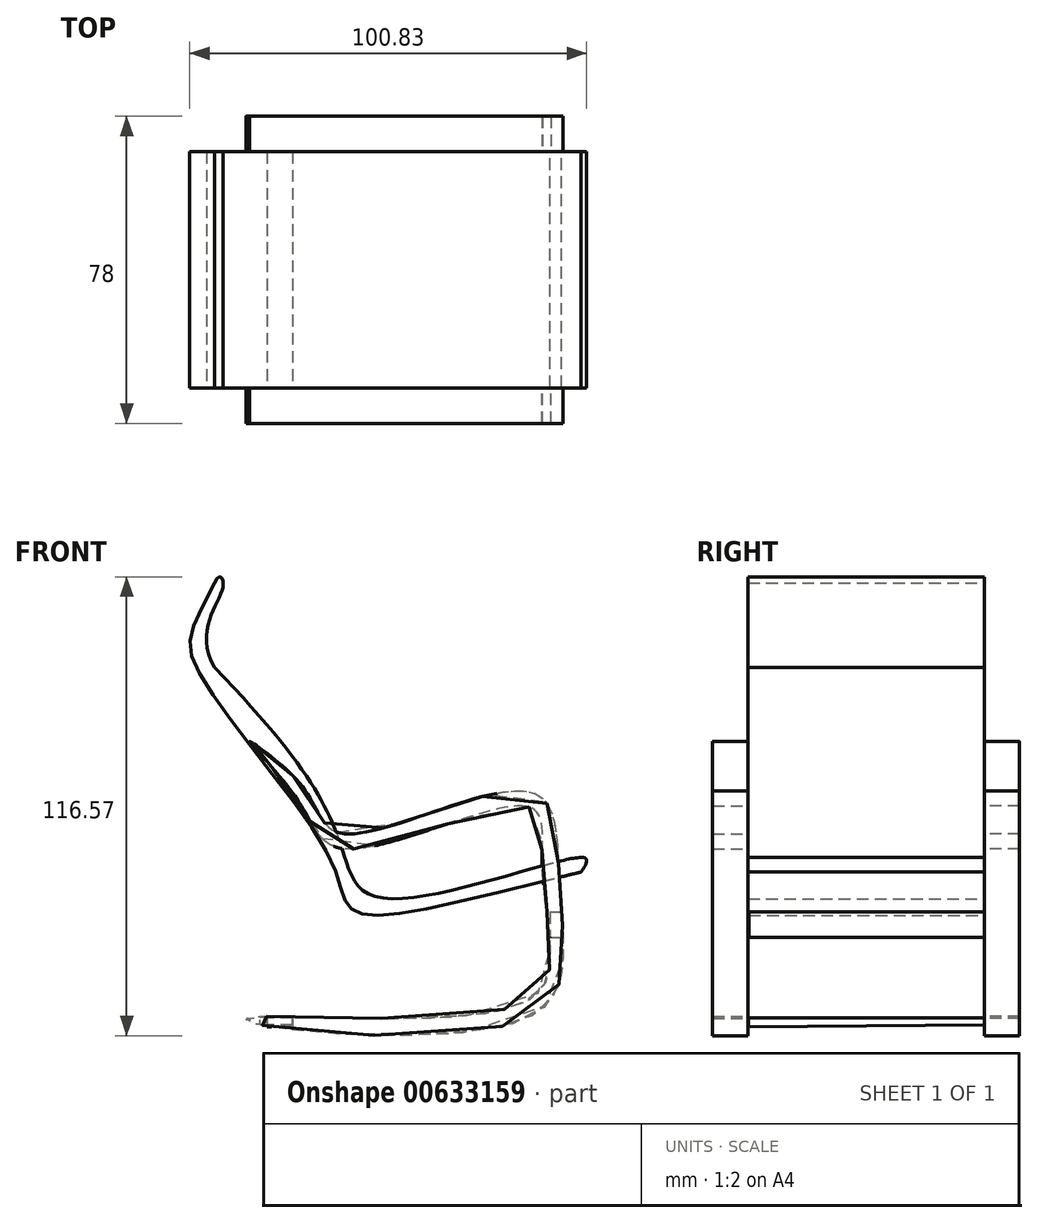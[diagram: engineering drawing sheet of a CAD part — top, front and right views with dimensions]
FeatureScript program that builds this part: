
annotation { "Feature Type Name" : "Feature", "Feature Type Description" : "" }
export const myFeature = defineFeature(function(context is Context, id is Id, definition is map)
    precondition{}
    {
        {
            var Q0;
            Q0=qCreatedBy(makeId("Front.planeOp"),FACE);
            var sketch = newSketch(context, id + "F0", { "sketchPlane" : qUnion([Q0])});
            skFitSpline(sketch, "E0", {"points": [v(-48.16, 69.9) * mm, v(-52.8, 48.36) * mm, v(-18.93, 0) * mm, v(-13.2, -13.17) * mm, v(44.92, -3.6) * mm], "startDerivative": vector(-88.69, -172.63) * mm, "endDerivative": vector(318.04, 76.89) * mm});
            skFitSpline(sketch, "E1", {"points": [v(-48.16, 69.9) * mm, v(-45.98, 69.9) * mm, v(-48.16, 48.36) * mm], "startDerivative": vector(13.48, 31.3) * mm, "endDerivative": vector(23, -40.33) * mm});
            skFitSpline(sketch, "E2", {"points": [v(-48.16, 48.36) * mm, v(-15.83, 2.51) * mm, v(-6.51, -10.03) * mm, v(43.68, 0) * mm, v(44.92, -3.6) * mm], "startDerivative": vector(188.22, -194.77) * mm, "endDerivative": vector(-82.48, -113.88) * mm});
            skSolve(sketch);
        }
        {
            var Q0;
            Q0=makeQuery(id+"F0.imprint","IMPRINT",FACE,{"disambiguationData":[TD([[makeQuery(id+"F0.imprint","IMPRINT",EDGE,{"derivedFrom":sQuery(id+"F0.wireOp",EDGE,"E0")}),1.0]])]});
            var Q1;
            Q1=sQuery(id+"F0.wireOp",EDGE,"E0");
            var Q2;
            Q2=sQuery(id+"F0.wireOp",EDGE,"E1");
            var Q3;
            Q3=sQuery(id+"F0.wireOp",EDGE,"E2");
            extrude(context, id + "F1", {"entities" : qUnion([Q0]), "surfaceEntities" : qUnion([Q1, Q2, Q3]), "depth" : 60 * mm, "offsetDistance" : 25 * mm});
        }
        {
            var Q0;
            Q0=qCreatedBy(makeId("Front.planeOp"),FACE);
            cPlane(context, id + "F2", {"entities" : qUnion([Q0]), "cplaneType" : CPlaneType.OFFSET, "offset" : 60 * mm, "width" : 150 * mm, "height" : 150 * mm});
        }
        {
            var Q0;
            Q0=qCreatedBy(id+"F2.planeOp",FACE);
            var sketch = newSketch(context, id + "F3", { "sketchPlane" : qUnion([Q0])});
            skFitSpline(sketch, "E3", {"points": [v(-38.56, 29.18) * mm, v(-25, 16.98) * mm, v(-15.26, 6.1) * mm, v(31.96, 16.75) * mm, v(39.1, 0) * mm, v(40.37, -22.89) * mm, v(30.08, -41.23) * mm, v(-39.86, -41.46) * mm, v(-39.86, -40.72) * mm, v(28.4, -37.68) * mm, v(37.18, -22.47) * mm, v(35.02, 0) * mm, v(31.8, 12.9) * mm, v(-14.68, 2.26) * mm, v(-27.1, 14.72) * mm, v(-39.28, 29.5) * mm, v(-38.56, 29.18) * mm]});
            skSolve(sketch);
        }
        {
            var Q0;
            Q0 = qSketchRegion(id + "F3", true);
            extrude(context, id + "F4", {"entities" : qUnion([Q0]), "operationType" : NewBodyOperationType.ADD, "depth" : 9 * mm, "offsetDistance" : 25 * mm});
        }
        {
            var Q0;
            Q0=qCreatedBy(makeId("Front.planeOp"),FACE);
            cPlane(context, id + "F5", {"entities" : qUnion([Q0]), "cplaneType" : CPlaneType.OFFSET, "offset" : 30 * mm, "width" : 150 * mm, "height" : 150 * mm});
        }
        {
            var Q0;
            Q0=makeQuery(id+"F1.opExtrude","SWEPT_BODY",BODY,{"disambiguationData":[OSD([sQuery(id+"F0.wireOp",EDGE,"E0"),sQuery(id+"F0.wireOp",EDGE,"E1"),sQuery(id+"F0.wireOp",EDGE,"E2")])]});
            var Q1;
            Q1=qCreatedBy(id+"F5.planeOp",FACE);
            mirror(context, id + "F6", {"operationType" : NewBodyOperationType.ADD, "entities" : qUnion([Q0]), "mirrorPlane" : qUnion([Q1])});
        }
        {
            var Q0;
            Q0=qCreatedBy(makeId("Right.planeOp"),FACE);
            cPlane(context, id + "F7", {"entities" : qUnion([Q0]), "cplaneType" : CPlaneType.OFFSET, "offset" : 40 * mm, "width" : 150 * mm, "height" : 150 * mm});
        }
        {
            var Q0;
            Q0=qCreatedBy(id+"F7.planeOp",FACE);
            var sketch = newSketch(context, id + "F8", { "sketchPlane" : qUnion([Q0])});
            skLineSegment(sketch, "E4", {"start": v(-59.8, -20.27) * mm, "end": v(0, -20.27) * mm});
            skLineSegment(sketch, "E5", {"start": v(-59.8, -20.27) * mm, "end": v(-59.8, -13.74) * mm});
            skLineSegment(sketch, "E6", {"start": v(-59.8, -13.74) * mm, "end": v(0, -13.74) * mm});
            skLineSegment(sketch, "E7", {"start": v(0, -13.74) * mm, "end": v(0, -20.27) * mm});
            skSolve(sketch);
        }
        {
            var Q0;
            Q0 = qSketchRegion(id + "F8", true);
            extrude(context, id + "F9", {"entities" : qUnion([Q0]), "operationType" : NewBodyOperationType.ADD, "oppositeDirection" : true, "depth" : 3 * mm, "offsetDistance" : 25 * mm});
        }
        {
            var Q0;
            Q0=qCreatedBy(makeId("Right.planeOp"),FACE);
            cPlane(context, id + "F10", {"entities" : qUnion([Q0]), "cplaneType" : CPlaneType.OFFSET, "offset" : 34.8 * mm, "oppositeDirection" : true, "width" : 150 * mm, "height" : 150 * mm});
        }
        {
            var Q0;
            Q0=qCreatedBy(id+"F10.planeOp",FACE);
            var sketch = newSketch(context, id + "F11", { "sketchPlane" : qUnion([Q0])});
            skLineSegment(sketch, "E8", {"start": v(-59.96, -43) * mm, "end": v(-59.96, -40.6) * mm});
            skLineSegment(sketch, "E9", {"start": v(-59.96, -40.6) * mm, "end": v(0, -40.6) * mm});
            skLineSegment(sketch, "E10", {"start": v(0, -40.6) * mm, "end": v(0, -42.48) * mm});
            skLineSegment(sketch, "E11", {"start": v(0, -42.48) * mm, "end": v(-59.96, -43) * mm});
            skSolve(sketch);
        }
        {
            var Q0;
            Q0 = qSketchRegion(id + "F11", true);
            extrude(context, id + "F12", {"entities" : qUnion([Q0]), "operationType" : NewBodyOperationType.ADD, "depth" : 6.4 * mm, "offsetDistance" : 25 * mm});
        }
    });
